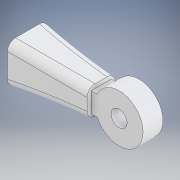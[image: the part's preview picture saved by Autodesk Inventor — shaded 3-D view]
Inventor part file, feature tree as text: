
AUTODESK INVENTOR PART (.ipt)
format: ipt  version: 2017 SP1 (Build 210196100, 196)  size: 198,656 bytes
history: native  units: in
note: dims shown in document units (in); Inventor stores cm internally (conversion verified against a paired STEP export)
features: extrude x7, sketch x7, projected_geometry x3, plane x1, fillet x1
ambient origin geometry x8: Origin, YZ Plane, XZ Plane, XY Plane, X Axis, Y Axis, Z Axis, Center Point
bodies: Solid1 (feature_tree)
feature tree (19):
  extrude  "Extrusion1"  Depth=0.4724in
  plane  "Work Plane1"
  extrude  "Extrusion2"  [1 undecoded]
  extrude  "Extrusion3"  Depth=0.1969in
  extrude  "Extrusion4"  Depth=0.6693in TaperAngle=0.0deg
  extrude  "Extrusion5"  Depth=0.3937in
  extrude  "Extrusion6"  Depth=11.811in
  fillet  "Fillet1"  Radius=11.811in
  extrude  "Extrusion7"  Depth=0.3937in
  sketch  "Sketch1"  dims[d0=0.1575in d1=0.4724in]
  sketch  "Sketch5"  dims[d2=0.1969in d3=0.0in d4=-0.0984in]
  sketch  "Sketch7"  dims[d5=0.1969in d6=0.1969in]
  projected_geometry  "Projected Loop2"
  sketch  "Sketch8"  dims[d7=0.2362in d8=0.0in d9=0.6693in d10=0.0in]
  sketch  "Sketch9"  dims[d11=0.3937in d12=0.2756in]
  sketch  "Sketch10"  dims[d13=0.2756in d14=11.811in d15=11.811in]
  projected_geometry  "Projected Loop3"
  projected_geometry  "Projected Loop4"
  sketch  "Sketch11"  dims[d16=0.2362in d17=0.0394in d18=0.0in d19=0.0in d20=0.3937in d21=11.811in d22=11.811in d23=0.0984in d24=0.2953in d25=0.0in d26=0.0in d27=0.0984in d28=0.0in d29=0.0787in d30=0.1181in d31=0.3937in d32=0.0in]
note: 1 required parameter value undecoded (feature->parameter linkage not recoverable at this tier; creation-order binding heuristic only, values carry confidence <= 0.55)
